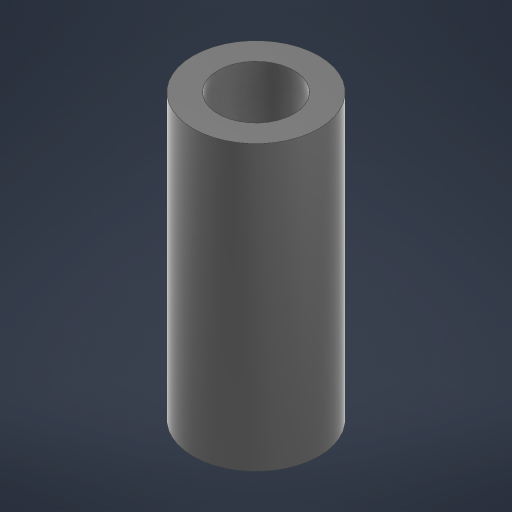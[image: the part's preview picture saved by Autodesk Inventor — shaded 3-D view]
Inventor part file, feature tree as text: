
AUTODESK INVENTOR PART (.ipt)
format: ipt  version: 2024.2 (Build 282272000, 272)  size: 176,128 bytes
history: native  units: mm
features: extrude x1, sketch x1, other x1
ambient origin geometry x8: Origin, YZ Plane, XZ Plane, XY Plane, X Axis, Y Axis, Z Axis, Center Point
bodies: Solid1 (feature_tree)
feature tree (3):
  extrude  "Extrusion1"  Depth=9.0mm
  sketch  "Sketch1"  dims[d0=2.4mm d1=4.0mm d2=9.0mm d3=0.0mm]
  other  "Finish1"
